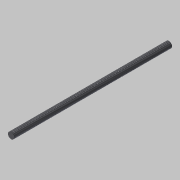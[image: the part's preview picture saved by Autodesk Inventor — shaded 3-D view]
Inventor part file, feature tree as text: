
AUTODESK INVENTOR PART (.ipt)
format: ipt  version: 2012 SP1 (Build 160190100, 190)  size: 68,608 bytes
history: native  units: in
note: dims shown in document units (in); Inventor stores cm internally (conversion verified against a paired STEP export)
features: extrude x1, thread x1, sketch x1
ambient origin geometry x8: Origin, YZ Plane, XZ Plane, XY Plane, X Axis, Y Axis, Z Axis, Center Point
bodies: Solid1 (feature_tree)
feature tree (3):
  extrude  "Extrusion1"  Depth=7.874in TaperAngle=0.0deg
  thread  "Thread1"  [1 undecoded]
  sketch  "Sketch1"  dims[d0=0.315in d1=7.874in d2=0.0in d3=1.0in d4=0.0in]
note: 1 required parameter value undecoded (feature->parameter linkage not recoverable at this tier; creation-order binding heuristic only, values carry confidence <= 0.55)
